# Revit family: Lockers_Cell_Phone-With_Access_Panel-Salsbury_Industries-Recessed_Mounted-7_Door_High_Units-8_Inch_Deep
name_source: partatom
category: Specialty Equipment
revit_build: Autodesk Revit 2016 (Build: 20190507_1515(x64)
units: mm (PartAtom-declared; Revit-internal decimal feet)

## family parameters
Cut with Voids When Loaded = No
Host = Face
OmniClass Number = 23.40.00.00
OmniClass Title = Equipment and Furnishings
Part Type = Normal
Room Calculation Point = No
Round Connector Dimension = Use Diameter
Shared = No

## types (8) — shared parameters
Assembly Code = C1030310
Assembly Description = Lockers
Back Enclosure Material = Aluminum - Salsbury Finish - Clear
Column Divider 1 = Yes
Column Divider 2 = Yes
Column Divider 3 = Yes
Depth = 8.75 "
Dial Numbering = Paint - Salsbury Finish - White
Door Slot L4 = A and B Access Doors : A Door - Access
Door Window Material = Plastic - Salsbury Finish - Clear
Height = 40.75 "
Lock Material = Stainless Steel - Salsbury Finish -  Polished
Manufacturer = Salsbury Industries
MasterFormat Number = 10 51 00
MasterFormat Title = Lockers
OmniClass 23 Number = 23.40.00.00
OmniClass 23 Title = Equipment and Furnishings
Resettable Combination Lock = Plastic - Salsbury Finish - Black
Row Divider 4 = Yes
Row Divider 5 = Yes
Row Divider 6 = Yes
Row Divider 7 = Yes
Type Comments = Cell Phone Lockers with Front Access Panel - Recessed Mounted Unit
URL = www.lockers.com
Version = 4.0 (03/09/21)
Visible Door Number = Yes

## per-type parameters (varying)
- 19178-35 with Keyed Locks: Column Divider 4=Yes; Column Divider 5=Yes; Description=35 A-Doors (34 Usable) with Keyed Locks - 7 Door High Unit; Door Slot L1=A and B Keyed Doors : A Door; Door Slot L10=A and B Keyed Doors : A Door; Door Slot L11=A and B Keyed Doors : A Door; Door Slot L12=A and B Keyed Doors : A Door; Door Slot L13=A and B Keyed Doors : A Door; Door Slot L14=A and B Keyed Doors : A Door; Door Slot L15=A and B Keyed Doors : A Door; Door Slot L16=A and B Keyed Doors : A Door; Door Slot L17=A and B Keyed Doors : A Door; Door Slot L18=A and B Keyed Doors : A Door; Door Slot L19=A and B Keyed Doors : A Door; Door Slot L2=A and B Keyed Doors : A Door; Door Slot L20=A and B Keyed Doors : A Door; Door Slot L21=A and B Keyed Doors : A Door; Door Slot L22=A and B Keyed Doors : A Door; Door Slot L23=A and B Keyed Doors : A Door; Door Slot L24=A and B Keyed Doors : A Door; Door Slot L25=A and B Keyed Doors : A Door; Door Slot L26=A and B Keyed Doors : A Door; Door Slot L27=A and B Keyed Doors : A Door; Door Slot L28=A and B Keyed Doors : A Door; Door Slot L29=A and B Keyed Doors : A Door; Door Slot L3=A and B Keyed Doors : A Door; Door Slot L30=A and B Keyed Doors : A Door; Door Slot L31=A and B Keyed Doors : A Door; Door Slot L32=A and B Keyed Doors : A Door; Door Slot L33=A and B Keyed Doors : A Door; Door Slot L34=A and B Keyed Doors : A Door; Door Slot L35=A and B Keyed Doors : A Door; Door Slot L5=A and B Keyed Doors : A Door; Door Slot L6=A and B Keyed Doors : A Door; Door Slot L7=A and B Keyed Doors : A Door; Door Slot L8=A and B Keyed Doors : A Door; Door Slot L9=A and B Keyed Doors : A Door; Model=19178-35; Rough Opening Width=34.75 "; Width=35.75 "
- 19178-24 with Keyed Locks: Column Divider 4=Yes; Column Divider 5=No; Description=20 A-Doors (19 Usable) and 4 B-Doors with Keyed Locks - 7 Door High Unit; Door Slot L1=A and B Keyed Doors : A Door; Door Slot L10=A and B Keyed Doors : A Door; Door Slot L11=A and B Keyed Doors : A Door; Door Slot L12=A and B Keyed Doors : A Door; Door Slot L13=A and B Keyed Doors : B Door; Door Slot L14=A and B Keyed Doors : B Door; Door Slot L15=A and B Keyed Doors : A Door; Door Slot L16=A and B Keyed Doors : A Door; Door Slot L17=A and B Keyed Doors : A Door; Door Slot L18=A and B Keyed Doors : A Door; Door Slot L19=A and B Keyed Doors : A Door; Door Slot L2=A and B Keyed Doors : A Door; Door Slot L20=A and B Keyed Doors : None; Door Slot L21=A and B Keyed Doors : None; Door Slot L22=A and B Keyed Doors : A Door; Door Slot L23=A and B Keyed Doors : A Door; Door Slot L24=A and B Keyed Doors : A Door; Door Slot L25=A and B Keyed Doors : A Door; Door Slot L26=A and B Keyed Doors : A Door; Door Slot L27=A and B Keyed Doors : B Door; Door Slot L28=A and B Keyed Doors : B Door; Door Slot L29=A and B Keyed Doors : None; Door Slot L3=A and B Keyed Doors : A Door; Door Slot L30=A and B Keyed Doors : None; Door Slot L31=A and B Keyed Doors : None; Door Slot L32=A and B Keyed Doors : None; Door Slot L33=A and B Keyed Doors : None; Door Slot L34=A and B Keyed Doors : None; Door Slot L35=A and B Keyed Doors : None; Door Slot L5=A and B Keyed Doors : A Door; Door Slot L6=A and B Keyed Doors : None; Door Slot L7=A and B Keyed Doors : None; Door Slot L8=A and B Keyed Doors : A Door; Door Slot L9=A and B Keyed Doors : A Door; Model=19178-24; Rough Opening Width=28.25 "; Width=29.25 "
- 19178-21 with Keyed Locks: Column Divider 4=No; Column Divider 5=No; Description=21 A-Doors (20 Usable) with Keyed Locks - 7 Door High Unit; Door Slot L1=A and B Keyed Doors : A Door; Door Slot L10=A and B Keyed Doors : A Door; Door Slot L11=A and B Keyed Doors : A Door; Door Slot L12=A and B Keyed Doors : A Door; Door Slot L13=A and B Keyed Doors : A Door; Door Slot L14=A and B Keyed Doors : A Door; Door Slot L15=A and B Keyed Doors : A Door; Door Slot L16=A and B Keyed Doors : A Door; Door Slot L17=A and B Keyed Doors : A Door; Door Slot L18=A and B Keyed Doors : A Door; Door Slot L19=A and B Keyed Doors : A Door; Door Slot L2=A and B Keyed Doors : A Door; Door Slot L20=A and B Keyed Doors : A Door; Door Slot L21=A and B Keyed Doors : A Door; Door Slot L22=A and B Keyed Doors : None; Door Slot L23=A and B Keyed Doors : None; Door Slot L24=A and B Keyed Doors : None; Door Slot L25=A and B Keyed Doors : None; Door Slot L26=A and B Keyed Doors : None; Door Slot L27=A and B Keyed Doors : None; Door Slot L28=A and B Keyed Doors : None; Door Slot L29=A and B Keyed Doors : None; Door Slot L3=A and B Keyed Doors : A Door; Door Slot L30=A and B Keyed Doors : None; Door Slot L31=A and B Keyed Doors : None; Door Slot L32=A and B Keyed Doors : None; Door Slot L33=A and B Keyed Doors : None; Door Slot L34=A and B Keyed Doors : None; Door Slot L35=A and B Keyed Doors : None; Door Slot L5=A and B Keyed Doors : A Door; Door Slot L6=A and B Keyed Doors : A Door; Door Slot L7=A and B Keyed Doors : A Door; Door Slot L8=A and B Keyed Doors : A Door; Door Slot L9=A and B Keyed Doors : A Door; Model=19178-21; Rough Opening Width=21.75 "; Width=22.75 "
- 19178-35 with Resettable Combination Locks: Column Divider 4=Yes; Column Divider 5=Yes; Description=35 A-Doors (34 Usable) with Resettable Combination Locks - 7 Door High Unit; Door Slot L1=A and B Combination Doors : A Door- Combination Lock; Door Slot L10=A and B Combination Doors : A Door- Combination Lock; Door Slot L11=A and B Combination Doors : A Door- Combination Lock; Door Slot L12=A and B Combination Doors : A Door- Combination Lock; Door Slot L13=A and B Combination Doors : A Door- Combination Lock; Door Slot L14=A and B Combination Doors : A Door- Combination Lock; Door Slot L15=A and B Combination Doors : A Door- Combination Lock; Door Slot L16=A and B Combination Doors : A Door- Combination Lock; Door Slot L17=A and B Combination Doors : A Door- Combination Lock; Door Slot L18=A and B Combination Doors : A Door- Combination Lock; Door Slot L19=A and B Combination Doors : A Door- Combination Lock; Door Slot L2=A and B Combination Doors : A Door- Combination Lock; Door Slot L20=A and B Combination Doors : A Door- Combination Lock; Door Slot L21=A and B Combination Doors : A Door- Combination Lock; Door Slot L22=A and B Combination Doors : A Door- Combination Lock; Door Slot L23=A and B Combination Doors : A Door- Combination Lock; Door Slot L24=A and B Combination Doors : A Door- Combination Lock; Door Slot L25=A and B Combination Doors : A Door- Combination Lock; Door Slot L26=A and B Combination Doors : A Door- Combination Lock; Door Slot L27=A and B Combination Doors : A Door- Combination Lock; Door Slot L28=A and B Combination Doors : A Door- Combination Lock; Door Slot L29=A and B Combination Doors : A Door- Combination Lock; Door Slot L3=A and B Combination Doors : A Door- Combination Lock; Door Slot L30=A and B Combination Doors : A Door- Combination Lock; Door Slot L31=A and B Combination Doors : A Door- Combination Lock; Door Slot L32=A and B Combination Doors : A Door- Combination Lock; Door Slot L33=A and B Combination Doors : A Door- Combination Lock; Door Slot L34=A and B Combination Doors : A Door- Combination Lock; Door Slot L35=A and B Combination Doors : A Door- Combination Lock; Door Slot L5=A and B Combination Doors : A Door- Combination Lock; Door Slot L6=A and B Combination Doors : A Door- Combination Lock; Door Slot L7=A and B Combination Doors : A Door- Combination Lock; Door Slot L8=A and B Combination Doors : A Door- Combination Lock; Door Slot L9=A and B Combination Doors : A Door- Combination Lock; Model=19178-35; Rough Opening Width=34.75 "; Width=35.75 "
- 19178-24 with Resettable Combination Locks: Column Divider 4=Yes; Column Divider 5=No; Description=20 A-Doors (19 Usable) and 4 B-Doors with Resettable Combination Locks - 7 Door High Unit; Door Slot L1=A and B Combination Doors : A Door- Combination Lock; Door Slot L10=A and B Combination Doors : A Door- Combination Lock; Door Slot L11=A and B Combination Doors : A Door- Combination Lock; Door Slot L12=A and B Combination Doors : A Door- Combination Lock; Door Slot L13=A and B Combination Doors : B Door - Combination Lock; Door Slot L14=A and B Combination Doors : B Door - Combination Lock; Door Slot L15=A and B Combination Doors : A Door- Combination Lock; Door Slot L16=A and B Combination Doors : A Door- Combination Lock; Door Slot L17=A and B Combination Doors : A Door- Combination Lock; Door Slot L18=A and B Combination Doors : A Door- Combination Lock; Door Slot L19=A and B Combination Doors : A Door- Combination Lock; Door Slot L2=A and B Combination Doors : A Door- Combination Lock; Door Slot L20=A and B Keyed Doors : None; Door Slot L21=A and B Keyed Doors : None; Door Slot L22=A and B Combination Doors : A Door- Combination Lock; Door Slot L23=A and B Combination Doors : A Door- Combination Lock; Door Slot L24=A and B Combination Doors : A Door- Combination Lock; Door Slot L25=A and B Combination Doors : A Door- Combination Lock; Door Slot L26=A and B Combination Doors : A Door- Combination Lock; Door Slot L27=A and B Combination Doors : B Door - Combination Lock; Door Slot L28=A and B Combination Doors : B Door - Combination Lock; Door Slot L29=A and B Keyed Doors : None; Door Slot L3=A and B Combination Doors : A Door- Combination Lock; Door Slot L30=A and B Keyed Doors : None; Door Slot L31=A and B Keyed Doors : None; Door Slot L32=A and B Keyed Doors : None; Door Slot L33=A and B Keyed Doors : None; Door Slot L34=A and B Keyed Doors : None; Door Slot L35=A and B Keyed Doors : None; Door Slot L5=A and B Combination Doors : A Door- Combination Lock; Door Slot L6=A and B Keyed Doors : None; Door Slot L7=A and B Keyed Doors : None; Door Slot L8=A and B Combination Doors : A Door- Combination Lock; Door Slot L9=A and B Combination Doors : A Door- Combination Lock; Model=19178-24; Rough Opening Width=28.25 "; Width=29.25 "
- 19178-21 with Resettable Combination Locks: Column Divider 4=No; Column Divider 5=No; Description=21 A-Doors (20 Usable) with Resettable Combination Locks - 7 Door High Unit; Door Slot L1=A and B Combination Doors : A Door- Combination Lock; Door Slot L10=A and B Combination Doors : A Door- Combination Lock; Door Slot L11=A and B Combination Doors : A Door- Combination Lock; Door Slot L12=A and B Combination Doors : A Door- Combination Lock; Door Slot L13=A and B Combination Doors : A Door- Combination Lock; Door Slot L14=A and B Combination Doors : A Door- Combination Lock; Door Slot L15=A and B Combination Doors : A Door- Combination Lock; Door Slot L16=A and B Combination Doors : A Door- Combination Lock; Door Slot L17=A and B Combination Doors : A Door- Combination Lock; Door Slot L18=A and B Combination Doors : A Door- Combination Lock; Door Slot L19=A and B Combination Doors : A Door- Combination Lock; Door Slot L2=A and B Combination Doors : A Door- Combination Lock; Door Slot L20=A and B Combination Doors : A Door- Combination Lock; Door Slot L21=A and B Combination Doors : A Door- Combination Lock; Door Slot L22=A and B Keyed Doors : None; Door Slot L23=A and B Keyed Doors : None; Door Slot L24=A and B Keyed Doors : None; Door Slot L25=A and B Keyed Doors : None; Door Slot L26=A and B Keyed Doors : None; Door Slot L27=A and B Keyed Doors : None; Door Slot L28=A and B Keyed Doors : None; Door Slot L29=A and B Keyed Doors : None; Door Slot L3=A and B Combination Doors : A Door- Combination Lock; Door Slot L30=A and B Keyed Doors : None; Door Slot L31=A and B Keyed Doors : None; Door Slot L32=A and B Keyed Doors : None; Door Slot L33=A and B Keyed Doors : None; Door Slot L34=A and B Keyed Doors : None; Door Slot L35=A and B Keyed Doors : None; Door Slot L5=A and B Combination Doors : A Door- Combination Lock; Door Slot L6=A and B Combination Doors : A Door- Combination Lock; Door Slot L7=A and B Combination Doors : A Door- Combination Lock; Door Slot L8=A and B Combination Doors : A Door- Combination Lock; Door Slot L9=A and B Combination Doors : A Door- Combination Lock; Model=19178-21; Rough Opening Width=21.75 "; Width=22.75 "
- 19178-28 with Resettable Combination Locks: Column Divider 4=Yes; Column Divider 5=No; Description=28 A-Doors (27 Usable) with Resettable Combination Locks - 7 Door High Unit; Door Slot L1=A and B Combination Doors : A Door- Combination Lock; Door Slot L10=A and B Combination Doors : A Door- Combination Lock; Door Slot L11=A and B Combination Doors : A Door- Combination Lock; Door Slot L12=A and B Combination Doors : A Door- Combination Lock; Door Slot L13=A and B Combination Doors : A Door- Combination Lock; Door Slot L14=A and B Combination Doors : A Door- Combination Lock; Door Slot L15=A and B Combination Doors : A Door- Combination Lock; Door Slot L16=A and B Combination Doors : A Door- Combination Lock; Door Slot L17=A and B Combination Doors : A Door- Combination Lock; Door Slot L18=A and B Combination Doors : A Door- Combination Lock; Door Slot L19=A and B Combination Doors : A Door- Combination Lock; Door Slot L2=A and B Combination Doors : A Door- Combination Lock; Door Slot L20=A and B Combination Doors : A Door- Combination Lock; Door Slot L21=A and B Combination Doors : A Door- Combination Lock; Door Slot L22=A and B Combination Doors : A Door- Combination Lock; Door Slot L23=A and B Combination Doors : A Door- Combination Lock; Door Slot L24=A and B Combination Doors : A Door- Combination Lock; Door Slot L25=A and B Combination Doors : A Door- Combination Lock; Door Slot L26=A and B Combination Doors : A Door- Combination Lock; Door Slot L27=A and B Combination Doors : A Door- Combination Lock; Door Slot L28=A and B Combination Doors : A Door- Combination Lock; Door Slot L29=A and B Keyed Doors : None; Door Slot L3=A and B Combination Doors : A Door- Combination Lock; Door Slot L30=A and B Keyed Doors : None; Door Slot L31=A and B Keyed Doors : None; Door Slot L32=A and B Keyed Doors : None; Door Slot L33=A and B Keyed Doors : None; Door Slot L34=A and B Keyed Doors : None; Door Slot L35=A and B Keyed Doors : None; Door Slot L5=A and B Combination Doors : A Door- Combination Lock; Door Slot L6=A and B Combination Doors : A Door- Combination Lock; Door Slot L7=A and B Combination Doors : A Door- Combination Lock; Door Slot L8=A and B Combination Doors : A Door- Combination Lock; Door Slot L9=A and B Combination Doors : A Door- Combination Lock; Model=19178-28; Rough Opening Width=28.25 "; Width=29.25 "
- 19178-28 with Keyed Locks: Column Divider 4=Yes; Column Divider 5=No; Description=28 A-Doors (27 Usable) with Keyed Locks - 7 Door High Unit; Door Slot L1=A and B Keyed Doors : A Door; Door Slot L10=A and B Keyed Doors : A Door; Door Slot L11=A and B Keyed Doors : A Door; Door Slot L12=A and B Keyed Doors : A Door; Door Slot L13=A and B Keyed Doors : A Door; Door Slot L14=A and B Keyed Doors : A Door; Door Slot L15=A and B Keyed Doors : A Door; Door Slot L16=A and B Keyed Doors : A Door; Door Slot L17=A and B Keyed Doors : A Door; Door Slot L18=A and B Keyed Doors : A Door; Door Slot L19=A and B Keyed Doors : A Door; Door Slot L2=A and B Keyed Doors : A Door; Door Slot L20=A and B Keyed Doors : A Door; Door Slot L21=A and B Keyed Doors : A Door; Door Slot L22=A and B Keyed Doors : A Door; Door Slot L23=A and B Keyed Doors : A Door; Door Slot L24=A and B Keyed Doors : A Door; Door Slot L25=A and B Keyed Doors : A Door; Door Slot L26=A and B Keyed Doors : A Door; Door Slot L27=A and B Keyed Doors : A Door; Door Slot L28=A and B Keyed Doors : A Door; Door Slot L29=A and B Keyed Doors : None; Door Slot L3=A and B Keyed Doors : A Door; Door Slot L30=A and B Keyed Doors : None; Door Slot L31=A and B Keyed Doors : None; Door Slot L32=A and B Keyed Doors : None; Door Slot L33=A and B Keyed Doors : None; Door Slot L34=A and B Keyed Doors : None; Door Slot L35=A and B Keyed Doors : None; Door Slot L5=A and B Keyed Doors : A Door; Door Slot L6=A and B Keyed Doors : A Door; Door Slot L7=A and B Keyed Doors : A Door; Door Slot L8=A and B Keyed Doors : A Door; Door Slot L9=A and B Keyed Doors : A Door; Model=19178-28; Rough Opening Width=28.25 "; Width=29.25 "

## geometry (parser evidence)
native form markers: Sweep x10
no freeform markers — native parametric forms only
